FCSTD DOCUMENT  (FreeCAD 0.14R2931 (Git))
Label: lengths
License: CC-BY 3.0
LicenseURL: http://creativecommons.org/licenses/by/3.0/
objects: Sketcher::SketchObject×1
note: 1 computed .brp shape members not serialized (recipe doc carries the construction recipe); baked Part::Feature solids carry a one-line shape summary decoded from their .brp

FEATURE [Sketcher::SketchObject] Sketch
  Placement = pos=(0,0,0) rot=(1,0,0;1.5708rad)
  sketch-geometry (38):
    g0: LineSegment StartX=-38.1 StartY=4.75 StartZ=0 EndX=38.1 EndY=4.75 EndZ=0
    g1: LineSegment StartX=38.1 StartY=4.75 StartZ=0 EndX=38.1 EndY=-4.75 EndZ=0
    g2: LineSegment StartX=38.1 StartY=-4.75 StartZ=0 EndX=-38.1 EndY=-4.75 EndZ=0
    g3: LineSegment StartX=-38.1 StartY=-4.75 StartZ=0 EndX=-38.1 EndY=4.75 EndZ=0
    g4: LineSegment [constr] StartX=0 StartY=0 StartZ=0 EndX=0 EndY=4.75 EndZ=0
    g5: LineSegment [constr] StartX=0 StartY=0 StartZ=0 EndX=-38.1 EndY=0 EndZ=0
    g6: LineSegment [constr] StartX=0 StartY=0 StartZ=0 EndX=38.1 EndY=0 EndZ=0
    g7: LineSegment [constr] StartX=0 StartY=0 StartZ=0 EndX=0 EndY=-4.75 EndZ=0
    g8: LineSegment StartX=38.1 StartY=-4.75 StartZ=0 EndX=46 EndY=-4.75 EndZ=0
    g9: LineSegment StartX=46 StartY=-4.75 StartZ=0 EndX=46 EndY=-7.13125 EndZ=0
    g10: LineSegment StartX=46 StartY=-7.13125 StartZ=0 EndX=-46 EndY=-7.13125 EndZ=0
    g11: LineSegment StartX=-46 StartY=-7.13125 StartZ=0 EndX=-46 EndY=-4.75 EndZ=0
    g12: LineSegment StartX=-46 StartY=-4.75 StartZ=0 EndX=-38.1 EndY=-4.75 EndZ=0
    g13: LineSegment StartX=-38.1 StartY=4.75 StartZ=0 EndX=-46 EndY=4.75 EndZ=0
    g14: LineSegment StartX=-46 StartY=4.75 StartZ=0 EndX=-46 EndY=7.13125 EndZ=0
    g15: LineSegment StartX=-46 StartY=7.13125 StartZ=0 EndX=46 EndY=7.13125 EndZ=0
    g16: LineSegment StartX=46 StartY=7.13125 StartZ=0 EndX=46 EndY=4.75 EndZ=0
    g17: LineSegment StartX=46 StartY=4.75 StartZ=0 EndX=38.1 EndY=4.75 EndZ=0
    g18: LineSegment StartX=46 StartY=7.13125 StartZ=0 EndX=49 EndY=7.13125 EndZ=0
    g19: LineSegment StartX=49 StartY=7.13125 StartZ=0 EndX=49 EndY=8.63125 EndZ=0
    g20: LineSegment StartX=49 StartY=8.63125 StartZ=0 EndX=-49 EndY=8.63125 EndZ=0
    g21: LineSegment StartX=-49 StartY=-8.63125 StartZ=0 EndX=49 EndY=-8.63125 EndZ=0
    g22: LineSegment StartX=49 StartY=-7.13125 StartZ=0 EndX=46 EndY=-7.13125 EndZ=0
    g23: LineSegment StartX=-46 StartY=-7.13125 StartZ=0 EndX=-49 EndY=-7.13125 EndZ=0
    g24: LineSegment StartX=-46 StartY=7.13125 StartZ=0 EndX=-49 EndY=7.13125 EndZ=0
    g25: LineSegment [constr] StartX=49 StartY=-7.13125 StartZ=0 EndX=49 EndY=-8.63125 EndZ=0
    g26: ArcOfCircle CenterX=-49 CenterY=0 CenterZ=0 NormalX=0 NormalY=0 NormalZ=1 Radius=7.13125 StartAngle=1.57079 EndAngle=4.71239
    g27: ArcOfCircle CenterX=-49 CenterY=0 CenterZ=0 NormalX=0 NormalY=0 NormalZ=1 Radius=8.63125 StartAngle=1.57079 EndAngle=4.71239
    g28: LineSegment [constr] StartX=-49 StartY=-7.13125 StartZ=0 EndX=-49 EndY=-8.63125 EndZ=0
    g29: Circle CenterX=-52.1313 CenterY=0 CenterZ=0 NormalX=0 NormalY=0 NormalZ=1 Radius=4
    g30: ArcOfCircle CenterX=49 CenterY=0.75 CenterZ=0 NormalX=0 NormalY=0 NormalZ=1 Radius=7.88125 StartAngle=4.71239 EndAngle=7.85398
    g31: ArcOfCircle CenterX=49 CenterY=0.75 CenterZ=0 NormalX=0 NormalY=0 NormalZ=1 Radius=9.38125 StartAngle=4.71239 EndAngle=7.85398
    g32: LineSegment [constr] StartX=49 StartY=-7.13125 StartZ=0 EndX=49 EndY=-8.63125 EndZ=0
    g33: LineSegment StartX=49 StartY=10.1312 StartZ=0 EndX=39 EndY=10.1312 EndZ=0
    g34: LineSegment [constr] StartX=39 StartY=10.1312 StartZ=0 EndX=39 EndY=8.63125 EndZ=0
    g35: LineSegment StartX=39 StartY=10.1312 StartZ=0 EndX=31 EndY=10.1312 EndZ=0
    g36: LineSegment StartX=31 StartY=10.1312 StartZ=0 EndX=31 EndY=8.63125 EndZ=0
    g37: ArcOfCircle CenterX=-55.2625 CenterY=0 CenterZ=0 NormalX=0 NormalY=0 NormalZ=1 Radius=7.13125 StartAngle=4.88766 EndAngle=7.67871
  constraints (114):
    c: Coincident(g0,g1)
    c: Coincident(g1,g2)
    c: Coincident(g2,g3)
    c: Coincident(g3,g0)
    c: Horizontal(g0)
    c: Horizontal(g2)
    c: Vertical(g1)
    c: Vertical(g3)
    c: DistanceX(g0) = 76.2
    c: Coincident(g4,g-1)
    c: PointOnObject(g4,g0)
    c: Vertical(g4)
    c: Coincident(g5,g-1)
    c: PointOnObject(g5,g3)
    c: Horizontal(g5)
    c: Coincident(g6,g-1)
    c: PointOnObject(g6,g1)
    c: Horizontal(g6)
    c: Coincident(g7,g-1)
    c: Vertical(g7)
    c: Equal(g7,g4)
    c: PointOnObject(g7,g2)
    c: Equal(g6,g5)
    c: DistanceY(g3) = 9.5
    c: Coincident(g1,g8)
    c: Horizontal(g8)
    c: Coincident(g8,g9)
    c: Vertical(g9)
    c: Coincident(g9,g10)
    c: Horizontal(g10)
    c: Coincident(g10,g11)
    c: Vertical(g11)
    c: Coincident(g11,g12)
    c: Coincident(g12,g2)
    c: Horizontal(g12)
    c: Equal(g12,g8)
    c: DistanceX(g10) = -92
    c: Coincident(g0,g13)
    c: Horizontal(g13)
    c: Coincident(g13,g14)
    c: Vertical(g14)
    c: Coincident(g14,g15)
    c: Horizontal(g15)
    c: Coincident(g15,g16)
    c: Vertical(g16)
    c: Coincident(g16,g17)
    c: Coincident(g17,g0)
    c: PointOnObject(g13,g11)
    c: Horizontal(g17)
    c: PointOnObject(g16,g9)
    c: Equal(g16,g9)
    c: DistanceY(g9) = -2.38125
    c: Coincident(g15,g18)
    c: Horizontal(g18)
    c: Coincident(g18,g19)
    c: Vertical(g19)
    c: Coincident(g19,g20)
    c: Horizontal(g20)
    c: Horizontal(g21)
    c: Coincident(g22,g9)
    c: Horizontal(g22)
    c: DistanceX(g18) = 3
    c: Coincident(g23,g10)
    c: Horizontal(g23)
    c: Equal(g23,g22)
    c: DistanceY(g22,g21) = -1.5
    c: Equal(g22,g18)
    c: Coincident(g24,g14)
    c: Horizontal(g24)
    c: Equal(g24,g18)
    c: Coincident(g25,g22)
    c: PointOnObject(g25,g21)
    c: Vertical(g25)
    c: Equal(g25,g19)
    c: Coincident(g26,g23)
    c: Coincident(g26,g24)
    c: Coincident(g27,g26)
    c: Coincident(g27,g20)
    c: Coincident(g27,g21)
    c: Coincident(g28,g23)
    c: PointOnObject(g28,g27)
    c: PointOnObject(g26,g28)
    c: Equal(g28,g25)
    c: PointOnObject(g29,g-1)
    c: Tangent(g29,g26)
    c: Radius(g29) = 4
    c: Coincident(g30,g22)
    c: Coincident(g30,g19)
    c: Coincident(g31,g30)
    c: Coincident(g31,g21)
    c: Coincident(g32,g22)
    c: PointOnObject(g32,g31)
    c: PointOnObject(g30,g32)
    c: Equal(g32,g25)
    c: Coincident(g33,g31)
    c: Horizontal(g33)
    c: Coincident(g34,g33)
    c: PointOnObject(g34,g20)
    c: Vertical(g34)
    c: DistanceX(g19,g34) = -10
    c: Coincident(g33,g35)
    c: Horizontal(g35)
    c: Coincident(g35,g36)
    c: PointOnObject(g36,g20)
    c: Vertical(g36)
    c: PointOnObject(g37,g-1)
    c: PointOnObject(g37,g27)
    c: PointOnObject(g37,g27)
    c: Tangent(g37,g29)
    c: Equal(g37,g26)
    c: Tangent(g27,g20)
    c: Equal(g36,g19)
    c: DistanceX(g35) = -8
    c: Tangent(g31,g33)
